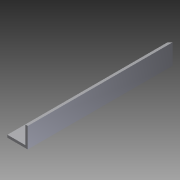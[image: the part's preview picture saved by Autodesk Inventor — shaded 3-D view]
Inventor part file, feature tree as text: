
AUTODESK INVENTOR PART (.ipt)
format: ipt  version: 2012 (Build 160160000, 160)  size: 81,408 bytes
history: native  units: in
note: dims shown in document units (in); Inventor stores cm internally (conversion verified against a paired STEP export)
features: extrude x2, sketch x2
ambient origin geometry x8: Origin, YZ Plane, XZ Plane, XY Plane, X Axis, Y Axis, Z Axis, Center Point
bodies: Solid1 (feature_tree)
feature tree (4):
  extrude  "Extrusion1"  Depth=1.0in
  extrude  "Extrusion2"  Depth=0.125in
  sketch  "Sketch1"  dims[d0=1.0in d1=1.0in]
  sketch  "Sketch2"  dims[d2=0.125in d3=0.125in d4=7.125in d5=0.0in d8=45.0deg d9=8.0in d10=0.0in]
